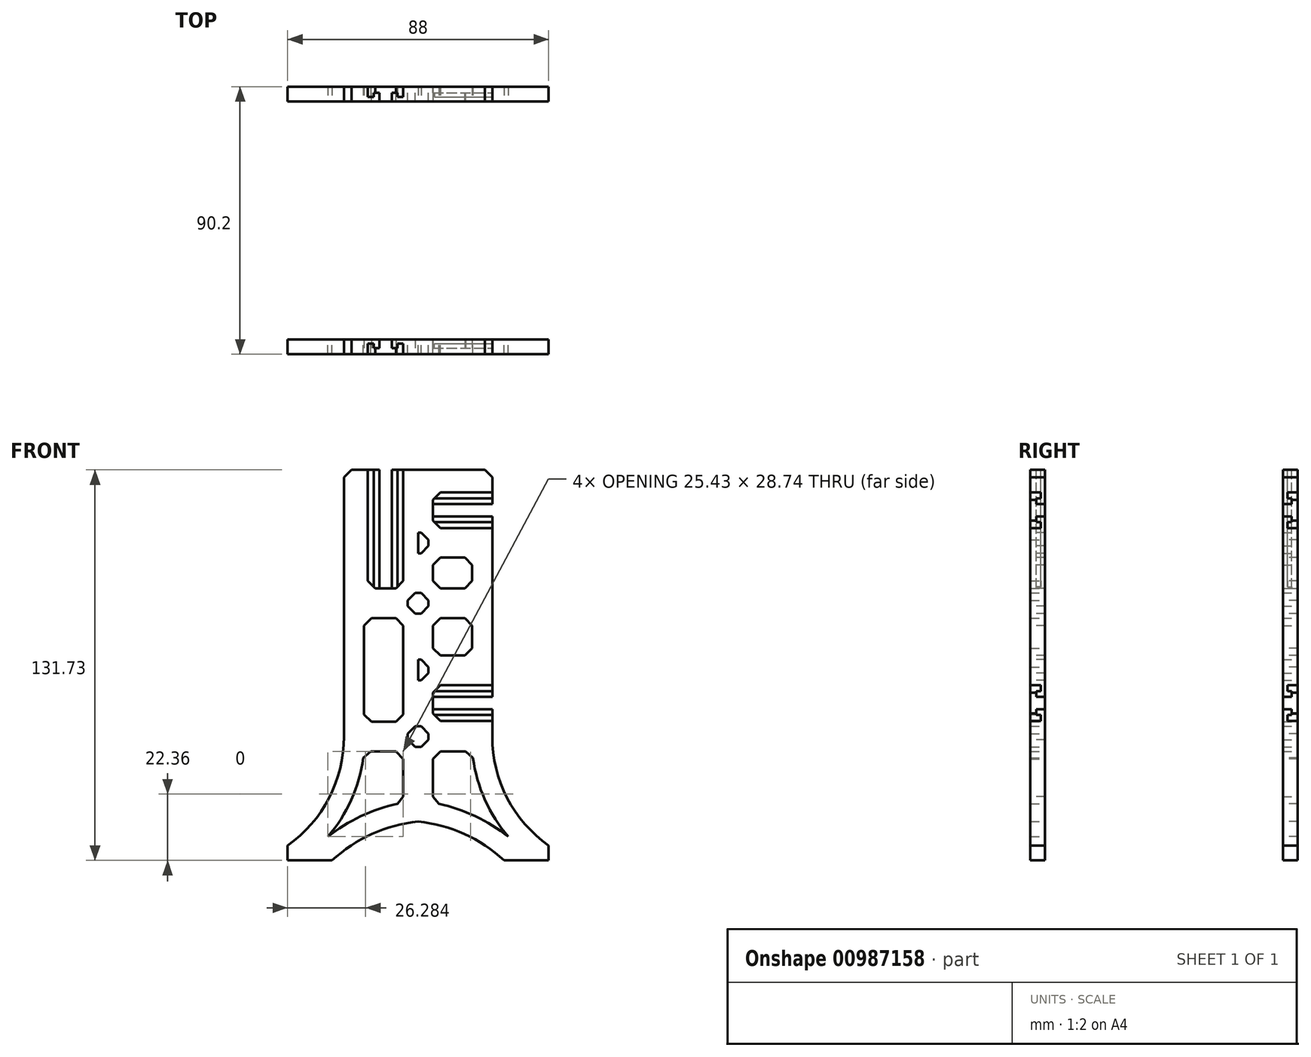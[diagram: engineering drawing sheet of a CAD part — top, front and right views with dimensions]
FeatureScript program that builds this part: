
annotation { "Feature Type Name" : "Feature", "Feature Type Description" : "" }
export const myFeature = defineFeature(function(context is Context, id is Id, definition is map)
    precondition{}
    {
        {
            var Q0;
            Q0=qCreatedBy(makeId("Front.planeOp"),FACE);
            var sketch = newSketch(context, id + "F0", { "sketchPlane" : qUnion([Q0])});
            skLineSegment(sketch, "E0", {"start": v(0, 90) * mm, "end": v(-25, 90) * mm});
            skLineSegment(sketch, "E1", {"start": v(-25, 90) * mm, "end": v(-25, 0) * mm});
            skLineSegment(sketch, "E2", {"start": v(-44, -41.73) * mm, "end": v(-29, -41.73) * mm});
            skLineSegment(sketch, "E3", {"start": v(-44, -41.73) * mm, "end": v(-44, -36.73) * mm});
            skArc(sketch, "E4", {"start": v(-25, 0) * mm, "mid": v(-30.03, -20.68) * mm, "end": v(-44, -36.73) * mm});
            skArc(sketch, "E5", {"start": v(0, -28.64) * mm, "mid": v(-15.57, -32.82) * mm, "end": v(-29, -41.73) * mm});
            skArc(sketch, "E6.0", {"start": v(-18.24, -5) * mm, "mid": v(-22.13, -20.3) * mm, "end": v(-30.43, -33.74) * mm});
            skArc(sketch, "E7.0", {"start": v(-5, -22.27) * mm, "mid": v(-18.43, -26.43) * mm, "end": v(-30.43, -33.74) * mm});
            skLineSegment(sketch, "E8", {"start": v(-18.24, -5) * mm, "end": v(-5, -5) * mm});
            skLineSegment(sketch, "E9", {"start": v(-5, -5) * mm, "end": v(-5, -22.27) * mm});
            skLineSegment(sketch, "E10", {"start": v(0, -28.64) * mm, "end": v(0, 90) * mm});
            skSolve(sketch);
        }
        {
            var Q0;
            Q0=makeQuery(id+"F0.imprint","IMPRINT",FACE,{"disambiguationData":[TD([[makeQuery(id+"F0.imprint","IMPRINT",EDGE,{"derivedFrom":sQuery(id+"F0.wireOp",EDGE,"E0")}),1.0]])]});
            extrude(context, id + "F1", {"entities" : qUnion([Q0]), "depth" : 5 * mm, "offsetDistance" : 25 * mm});
        }
        {
            var Q0;
            Q0=makeQuery(id+"F1.opExtrude","SWEPT_BODY",BODY,{"disambiguationData":[OSD([sQuery(id+"F0.wireOp",EDGE,"E0"),sQuery(id+"F0.wireOp",EDGE,"E1"),sQuery(id+"F0.wireOp",EDGE,"E2"),sQuery(id+"F0.wireOp",EDGE,"E3"),sQuery(id+"F0.wireOp",EDGE,"E4"),sQuery(id+"F0.wireOp",EDGE,"E5"),sQuery(id+"F0.wireOp",EDGE,"E6.0"),sQuery(id+"F0.wireOp",EDGE,"E7.0"),sQuery(id+"F0.wireOp",EDGE,"E8"),sQuery(id+"F0.wireOp",EDGE,"E9"),sQuery(id+"F0.wireOp",EDGE,"E10")])]});
            var Q1;
            Q1=qCreatedBy(makeId("Right.planeOp"),FACE);
            mirror(context, id + "F2", {"operationType" : NewBodyOperationType.ADD, "entities" : qUnion([Q0]), "mirrorPlane" : qUnion([Q1])});
        }
        {
            var Q0;
            Q0=makeQuery(id+"F2.opPattern","COPY",FACE,{"derivedFrom":makeQuery(id+"F1.opExtrude","SWEPT_FACE",FACE,{"disambiguationData":[OSD([sQuery(id+"F0.wireOp",EDGE,"E1")])]}),"instanceName":"1"});
            var sketch = newSketch(context, id + "F3", { "sketchPlane" : qUnion([Q0])});
            skLineSegment(sketch, "E11", {"start": v(0, 11.37) * mm, "end": v(-5, 11.37) * mm, "construction": true});
            skLineSegment(sketch, "E12", {"start": v(-5, 11.37) * mm, "end": v(-5, 17.37) * mm});
            skLineSegment(sketch, "E13", {"start": v(-5, 17.37) * mm, "end": v(-1.5, 17.37) * mm});
            skLineSegment(sketch, "E14", {"start": v(-1.5, 17.37) * mm, "end": v(-1.5, 15.37) * mm});
            skLineSegment(sketch, "E15", {"start": v(-1.5, 15.37) * mm, "end": v(-3, 15.37) * mm});
            skLineSegment(sketch, "E16", {"start": v(-3, 15.37) * mm, "end": v(-3, 13.47) * mm});
            skLineSegment(sketch, "E17", {"start": v(-3, 13.47) * mm, "end": v(0, 13.47) * mm});
            skLineSegment(sketch, "E18", {"start": v(0, 13.47) * mm, "end": v(0, 11.37) * mm});
            skLineSegment(sketch, "E19.MirrorCS", {"start": v(-3, 9.27) * mm, "end": v(0, 9.27) * mm});
            skLineSegment(sketch, "E20.MirrorCS", {"start": v(0, 9.27) * mm, "end": v(0, 11.37) * mm});
            skLineSegment(sketch, "E21.MirrorCS", {"start": v(-5, 5.37) * mm, "end": v(-1.5, 5.37) * mm});
            skLineSegment(sketch, "E22.MirrorCS", {"start": v(-5, 11.37) * mm, "end": v(-5, 5.37) * mm});
            skLineSegment(sketch, "E23.MirrorCS", {"start": v(-3, 7.37) * mm, "end": v(-3, 9.27) * mm});
            skLineSegment(sketch, "E24.MirrorCS", {"start": v(-1.5, 5.37) * mm, "end": v(-1.5, 7.37) * mm});
            skLineSegment(sketch, "E25.MirrorCS", {"start": v(-1.5, 7.37) * mm, "end": v(-3, 7.37) * mm});
            skLineSegment(sketch, "E26.0.1.0", {"start": v(-5, 76.37) * mm, "end": v(-5, 70.37) * mm});
            skLineSegment(sketch, "E26.0.1.1", {"start": v(-3, 74.27) * mm, "end": v(0, 74.27) * mm});
            skLineSegment(sketch, "E26.0.1.2", {"start": v(0, 76.37) * mm, "end": v(-5, 76.37) * mm, "construction": true});
            skLineSegment(sketch, "E26.0.1.3", {"start": v(-5, 82.37) * mm, "end": v(-1.5, 82.37) * mm});
            skLineSegment(sketch, "E26.0.1.4", {"start": v(-5, 76.37) * mm, "end": v(-5, 82.37) * mm});
            skLineSegment(sketch, "E26.0.1.5", {"start": v(-5, 70.37) * mm, "end": v(-1.5, 70.37) * mm});
            skLineSegment(sketch, "E26.0.1.6", {"start": v(-3, 78.47) * mm, "end": v(0, 78.47) * mm});
            skLineSegment(sketch, "E26.0.1.7", {"start": v(-1.5, 70.37) * mm, "end": v(-1.5, 72.37) * mm});
            skLineSegment(sketch, "E26.0.1.8", {"start": v(0, 74.27) * mm, "end": v(0, 76.37) * mm});
            skLineSegment(sketch, "E26.0.1.9", {"start": v(-3, 80.37) * mm, "end": v(-3, 78.47) * mm});
            skLineSegment(sketch, "E26.0.1.10", {"start": v(-3, 72.37) * mm, "end": v(-3, 74.27) * mm});
            skLineSegment(sketch, "E26.0.1.11", {"start": v(0, 78.47) * mm, "end": v(0, 76.37) * mm});
            skLineSegment(sketch, "E26.0.1.12", {"start": v(-1.5, 82.37) * mm, "end": v(-1.5, 80.37) * mm});
            skLineSegment(sketch, "E26.0.1.13", {"start": v(-1.5, 72.37) * mm, "end": v(-3, 72.37) * mm});
            skLineSegment(sketch, "E26.0.1.14", {"start": v(-1.5, 80.37) * mm, "end": v(-3, 80.37) * mm});
            skLineSegment(sketch, "E26.direction1", {"start": v(-5, 5.37) * mm, "end": v(20, 5.37) * mm, "construction": true});
            skLineSegment(sketch, "E26.direction2", {"start": v(-5, 5.37) * mm, "end": v(-5, 70.37) * mm, "construction": true});
            skSolve(sketch);
        }
        {
            var Q0;
            Q0=makeQuery(id+"F3.imprint","IMPRINT",FACE,{"disambiguationData":[TD([[makeQuery(id+"F3.imprint","IMPRINT",EDGE,{"derivedFrom":sQuery(id+"F3.wireOp",EDGE,"E26.0.1.0")}),1.0]])]});
            var Q1;
            Q1=makeQuery(id+"F3.imprint","IMPRINT",FACE,{"disambiguationData":[TD([[makeQuery(id+"F3.imprint","IMPRINT",EDGE,{"derivedFrom":sQuery(id+"F3.wireOp",EDGE,"E12")}),1.0]])]});
            extrude(context, id + "F4", {"entities" : qUnion([Q0, Q1]), "operationType" : NewBodyOperationType.REMOVE, "oppositeDirection" : true, "depth" : 20 * mm, "offsetDistance" : 25 * mm});
        }
        {
            var Q0;
            {var subQ0=makeQuery(id+"F1.opExtrude","SWEPT_FACE",FACE,{"disambiguationData":[OSD([sQuery(id+"F0.wireOp",EDGE,"E0")])]});Q0=makeQuery(id+"F2.boolean.opBoolean","MERGE",FACE,{"derivedFrom":[subQ0,makeQuery(id+"F2.opPattern","COPY",FACE,{"derivedFrom":subQ0,"instanceName":"1"})]});}
            var sketch = newSketch(context, id + "F5", { "sketchPlane" : qUnion([Q0])});
            skLineSegment(sketch, "E27", {"start": v(-17, -1.5) * mm, "end": v(-17, -5) * mm});
            skLineSegment(sketch, "E28", {"start": v(-17, -5) * mm, "end": v(-11, -5) * mm});
            skLineSegment(sketch, "E29", {"start": v(-11, -5) * mm, "end": v(-11, 0) * mm, "construction": true});
            skLineSegment(sketch, "E30", {"start": v(-11, 0) * mm, "end": v(-13.1, 0) * mm});
            skLineSegment(sketch, "E31", {"start": v(-13.1, 0) * mm, "end": v(-13.1, -3) * mm});
            skLineSegment(sketch, "E32", {"start": v(-13.1, -3) * mm, "end": v(-15, -3) * mm});
            skLineSegment(sketch, "E33", {"start": v(-15, -3) * mm, "end": v(-15, -1.5) * mm});
            skLineSegment(sketch, "E34", {"start": v(-15, -1.5) * mm, "end": v(-17, -1.5) * mm});
            skLineSegment(sketch, "E35.MirrorCS", {"start": v(-8.9, 0) * mm, "end": v(-8.9, -3) * mm});
            skLineSegment(sketch, "E36.MirrorCS", {"start": v(-7, -3) * mm, "end": v(-7, -1.5) * mm});
            skLineSegment(sketch, "E37.MirrorCS", {"start": v(-5, -5) * mm, "end": v(-11, -5) * mm});
            skLineSegment(sketch, "E38.MirrorCS", {"start": v(-11, 0) * mm, "end": v(-8.9, 0) * mm});
            skLineSegment(sketch, "E39.MirrorCS", {"start": v(-8.9, -3) * mm, "end": v(-7, -3) * mm});
            skLineSegment(sketch, "E40.MirrorCS", {"start": v(-7, -1.5) * mm, "end": v(-5, -1.5) * mm});
            skLineSegment(sketch, "E41.MirrorCS", {"start": v(-5, -1.5) * mm, "end": v(-5, -5) * mm});
            skSolve(sketch);
        }
        {
            var Q0;
            Q0=makeQuery(id+"F5.imprint","IMPRINT",FACE,{"disambiguationData":[TD([[makeQuery(id+"F5.imprint","IMPRINT",EDGE,{"derivedFrom":sQuery(id+"F5.wireOp",EDGE,"E27")}),1.0]])]});
            extrude(context, id + "F6", {"entities" : qUnion([Q0]), "operationType" : NewBodyOperationType.REMOVE, "oppositeDirection" : true, "depth" : 40 * mm, "offsetDistance" : 25 * mm});
        }
        {
            var Q0;
            {var subQ0=makeQuery(id+"F1.opExtrude","CAP_FACE",FACE,{"disambiguationData":[OSD([sQuery(id+"F0.wireOp",EDGE,"E0"),sQuery(id+"F0.wireOp",EDGE,"E1"),sQuery(id+"F0.wireOp",EDGE,"E2"),sQuery(id+"F0.wireOp",EDGE,"E3"),sQuery(id+"F0.wireOp",EDGE,"E4"),sQuery(id+"F0.wireOp",EDGE,"E5"),sQuery(id+"F0.wireOp",EDGE,"E6.0"),sQuery(id+"F0.wireOp",EDGE,"E7.0"),sQuery(id+"F0.wireOp",EDGE,"E8"),sQuery(id+"F0.wireOp",EDGE,"E9"),sQuery(id+"F0.wireOp",EDGE,"E10")])],"isStart":false});Q0=makeQuery(id+"F2.boolean.opBoolean","MERGE",FACE,{"derivedFrom":[subQ0,makeQuery(id+"F2.opPattern","COPY",FACE,{"derivedFrom":subQ0,"instanceName":"1"})]});}
            var sketch = newSketch(context, id + "F7", { "sketchPlane" : qUnion([Q0])});
            skLineSegment(sketch, "E42.bottom", {"start": v(-18.24, 5) * mm, "end": v(-5, 5) * mm});
            skLineSegment(sketch, "E42.top", {"start": v(-18.24, 40) * mm, "end": v(-5, 40) * mm});
            skLineSegment(sketch, "E42.left", {"start": v(-18.24, 5) * mm, "end": v(-18.24, 40) * mm});
            skLineSegment(sketch, "E42.right", {"start": v(-5, 5) * mm, "end": v(-5, 40) * mm});
            skLineSegment(sketch, "E43.bottom", {"start": v(5, 40) * mm, "end": v(18.24, 40) * mm});
            skLineSegment(sketch, "E43.top", {"start": v(5, 27.37) * mm, "end": v(18.24, 27.37) * mm});
            skLineSegment(sketch, "E43.left", {"start": v(5, 40) * mm, "end": v(5, 27.37) * mm});
            skLineSegment(sketch, "E43.right", {"start": v(18.24, 40) * mm, "end": v(18.24, 27.37) * mm});
            skLineSegment(sketch, "E44.bottom", {"start": v(5, 60.37) * mm, "end": v(18.24, 60.37) * mm});
            skLineSegment(sketch, "E44.top", {"start": v(5, 50) * mm, "end": v(18.24, 50) * mm});
            skLineSegment(sketch, "E44.left", {"start": v(5, 60.37) * mm, "end": v(5, 50) * mm});
            skLineSegment(sketch, "E44.right", {"start": v(18.24, 60.37) * mm, "end": v(18.24, 50) * mm});
            skLineSegment(sketch, "E45.bottom", {"start": v(3.5, 41.5) * mm, "end": v(-3.5, 41.5) * mm});
            skLineSegment(sketch, "E45.top", {"start": v(3.5, 48.5) * mm, "end": v(-3.5, 48.5) * mm});
            skLineSegment(sketch, "E45.left", {"start": v(3.5, 41.5) * mm, "end": v(3.5, 48.5) * mm});
            skLineSegment(sketch, "E45.right", {"start": v(-3.5, 41.5) * mm, "end": v(-3.5, 48.5) * mm});
            skPoint(sketch, "E45.middle", {"position": v(0, 45) * mm});
            skLineSegment(sketch, "E46", {"start": v(-5, 22.5) * mm, "end": v(-18.24, 22.5) * mm, "construction": true});
            skLineSegment(sketch, "E47.MirrorCS", {"start": v(3.5, 3.5) * mm, "end": v(3.5, -3.5) * mm});
            skPoint(sketch, "E48.MirrorP", {"position": v(0, 0) * mm});
            skLineSegment(sketch, "E49.MirrorCS", {"start": v(3.5, 3.5) * mm, "end": v(-3.5, 3.5) * mm});
            skLineSegment(sketch, "E50.MirrorCS", {"start": v(3.5, -3.5) * mm, "end": v(-3.5, -3.5) * mm});
            skLineSegment(sketch, "E51.MirrorCS", {"start": v(-3.5, 3.5) * mm, "end": v(-3.5, -3.5) * mm});
            skLineSegment(sketch, "E52.bottom", {"start": v(0, 26) * mm, "end": v(3.5, 26) * mm});
            skLineSegment(sketch, "E52.top", {"start": v(0, 19) * mm, "end": v(3.5, 19) * mm});
            skLineSegment(sketch, "E52.left", {"start": v(0, 26) * mm, "end": v(0, 19) * mm});
            skLineSegment(sketch, "E52.right", {"start": v(3.5, 26) * mm, "end": v(3.5, 19) * mm});
            skPoint(sketch, "E53", {"position": v(0, 22.5) * mm});
            skLineSegment(sketch, "E54.bottom", {"start": v(0, 68.87) * mm, "end": v(3.5, 68.87) * mm});
            skLineSegment(sketch, "E54.top", {"start": v(0, 61.87) * mm, "end": v(3.5, 61.87) * mm});
            skLineSegment(sketch, "E54.left", {"start": v(0, 68.87) * mm, "end": v(0, 61.87) * mm});
            skLineSegment(sketch, "E54.right", {"start": v(3.5, 68.87) * mm, "end": v(3.5, 61.87) * mm});
            skPoint(sketch, "E55", {"position": v(0, 65.37) * mm});
            skSolve(sketch);
        }
        {
            var Q0;
            Q0=makeQuery(id+"F7.imprint","IMPRINT",FACE,{"disambiguationData":[TD([[makeQuery(id+"F7.imprint","IMPRINT",EDGE,{"derivedFrom":sQuery(id+"F7.wireOp",EDGE,"E42.bottom")}),1.0]])]});
            var Q1;
            Q1=makeQuery(id+"F7.imprint","IMPRINT",FACE,{"disambiguationData":[TD([[makeQuery(id+"F7.imprint","IMPRINT",EDGE,{"derivedFrom":sQuery(id+"F7.wireOp",EDGE,"E43.bottom")}),-1.0]])]});
            var Q2;
            Q2=makeQuery(id+"F7.imprint","IMPRINT",FACE,{"disambiguationData":[TD([[makeQuery(id+"F7.imprint","IMPRINT",EDGE,{"derivedFrom":sQuery(id+"F7.wireOp",EDGE,"E44.bottom")}),-1.0]])]});
            var Q3;
            Q3=makeQuery(id+"F7.imprint","IMPRINT",FACE,{"disambiguationData":[TD([[makeQuery(id+"F7.imprint","IMPRINT",EDGE,{"derivedFrom":sQuery(id+"F7.wireOp",EDGE,"E45.bottom")}),-1.0]])]});
            var Q4;
            Q4=makeQuery(id+"F7.imprint","IMPRINT",FACE,{"disambiguationData":[TD([[makeQuery(id+"F7.imprint","IMPRINT",EDGE,{"derivedFrom":sQuery(id+"F7.wireOp",EDGE,"E47.MirrorCS")}),-1.0]])]});
            var Q5;
            Q5=makeQuery(id+"F7.imprint","IMPRINT",FACE,{"disambiguationData":[TD([[makeQuery(id+"F7.imprint","IMPRINT",EDGE,{"derivedFrom":sQuery(id+"F7.wireOp",EDGE,"E54.bottom")}),-1.0]])]});
            var Q6;
            Q6=makeQuery(id+"F7.imprint","IMPRINT",FACE,{"disambiguationData":[TD([[makeQuery(id+"F7.imprint","IMPRINT",EDGE,{"derivedFrom":sQuery(id+"F7.wireOp",EDGE,"E52.bottom")}),-1.0]])]});
            extrude(context, id + "F8", {"entities" : qUnion([Q0, Q1, Q2, Q3, Q4, Q5, Q6]), "operationType" : NewBodyOperationType.REMOVE, "endBound" : BoundingType.THROUGH_ALL, "oppositeDirection" : true, "depth" : 25 * mm, "offsetDistance" : 25 * mm});
        }
        {
            var Q0;
            Q0=makeQuery(id+"F1.opExtrude","SWEPT_EDGE",EDGE,{"disambiguationData":[OSD([sQuery(id+"F0.wireOp",EDGE,"E8"),sQuery(id+"F0.wireOp",EDGE,"E9")])]});
            var Q1;
            Q1=makeQuery(id+"F1.opExtrude","SWEPT_EDGE",EDGE,{"disambiguationData":[OSD([sQuery(id+"F0.wireOp",EDGE,"E6.0"),sQuery(id+"F0.wireOp",EDGE,"E8")])]});
            var Q2;
            Q2=makeQuery(id+"F1.opExtrude","SWEPT_EDGE",EDGE,{"disambiguationData":[OSD([sQuery(id+"F0.wireOp",EDGE,"E7.0"),sQuery(id+"F0.wireOp",EDGE,"E9")])]});
            var Q3;
            Q3=makeQuery(id+"F2.opPattern","COPY",EDGE,{"derivedFrom":makeQuery(id+"F1.opExtrude","SWEPT_EDGE",EDGE,{"disambiguationData":[OSD([sQuery(id+"F0.wireOp",EDGE,"E7.0"),sQuery(id+"F0.wireOp",EDGE,"E9")])]}),"instanceName":"1"});
            var Q4;
            Q4=makeQuery(id+"F2.opPattern","COPY",EDGE,{"derivedFrom":makeQuery(id+"F1.opExtrude","SWEPT_EDGE",EDGE,{"disambiguationData":[OSD([sQuery(id+"F0.wireOp",EDGE,"E8"),sQuery(id+"F0.wireOp",EDGE,"E9")])]}),"instanceName":"1"});
            var Q5;
            Q5=makeQuery(id+"F2.opPattern","COPY",EDGE,{"derivedFrom":makeQuery(id+"F1.opExtrude","SWEPT_EDGE",EDGE,{"disambiguationData":[OSD([sQuery(id+"F0.wireOp",EDGE,"E6.0"),sQuery(id+"F0.wireOp",EDGE,"E8")])]}),"instanceName":"1"});
            var Q6;
            Q6=makeQuery(id+"F8.boolean.opBoolean","COPY",EDGE,{"derivedFrom":makeQuery(id+"F8.opExtrude","SWEPT_EDGE",EDGE,{"disambiguationData":[OSD([sQuery(id+"F7.wireOp",EDGE,"E42.bottom"),sQuery(id+"F7.wireOp",EDGE,"E42.right")])]})});
            var Q7;
            Q7=makeQuery(id+"F8.boolean.opBoolean","COPY",EDGE,{"derivedFrom":makeQuery(id+"F8.opExtrude","SWEPT_EDGE",EDGE,{"disambiguationData":[OSD([sQuery(id+"F7.wireOp",EDGE,"E42.bottom"),sQuery(id+"F7.wireOp",EDGE,"E42.left")])]})});
            var Q8;
            Q8=makeQuery(id+"F8.boolean.opBoolean","COPY",EDGE,{"derivedFrom":makeQuery(id+"F8.opExtrude","SWEPT_EDGE",EDGE,{"disambiguationData":[OSD([sQuery(id+"F7.wireOp",EDGE,"E42.top"),sQuery(id+"F7.wireOp",EDGE,"E42.left")])]})});
            var Q9;
            Q9=makeQuery(id+"F8.boolean.opBoolean","COPY",EDGE,{"derivedFrom":makeQuery(id+"F8.opExtrude","SWEPT_EDGE",EDGE,{"disambiguationData":[OSD([sQuery(id+"F7.wireOp",EDGE,"E42.top"),sQuery(id+"F7.wireOp",EDGE,"E42.right")])]})});
            var Q10;
            Q10=makeQuery(id+"F8.boolean.opBoolean","COPY",EDGE,{"derivedFrom":makeQuery(id+"F8.opExtrude","SWEPT_EDGE",EDGE,{"disambiguationData":[OSD([sQuery(id+"F7.wireOp",EDGE,"E43.bottom"),sQuery(id+"F7.wireOp",EDGE,"E43.left")])]})});
            var Q11;
            Q11=makeQuery(id+"F8.boolean.opBoolean","COPY",EDGE,{"derivedFrom":makeQuery(id+"F8.opExtrude","SWEPT_EDGE",EDGE,{"disambiguationData":[OSD([sQuery(id+"F7.wireOp",EDGE,"E44.top"),sQuery(id+"F7.wireOp",EDGE,"E44.left")])]})});
            var Q12;
            Q12=makeQuery(id+"F8.boolean.opBoolean","COPY",EDGE,{"derivedFrom":makeQuery(id+"F8.opExtrude","SWEPT_EDGE",EDGE,{"disambiguationData":[OSD([sQuery(id+"F7.wireOp",EDGE,"E44.bottom"),sQuery(id+"F7.wireOp",EDGE,"E44.left")])]})});
            var Q13;
            Q13=makeQuery(id+"F8.boolean.opBoolean","COPY",EDGE,{"derivedFrom":makeQuery(id+"F8.opExtrude","SWEPT_EDGE",EDGE,{"disambiguationData":[OSD([sQuery(id+"F7.wireOp",EDGE,"E44.bottom"),sQuery(id+"F7.wireOp",EDGE,"E44.right")])]})});
            var Q14;
            Q14=makeQuery(id+"F8.boolean.opBoolean","COPY",EDGE,{"derivedFrom":makeQuery(id+"F8.opExtrude","SWEPT_EDGE",EDGE,{"disambiguationData":[OSD([sQuery(id+"F7.wireOp",EDGE,"E44.top"),sQuery(id+"F7.wireOp",EDGE,"E44.right")])]})});
            var Q15;
            Q15=makeQuery(id+"F8.boolean.opBoolean","COPY",EDGE,{"derivedFrom":makeQuery(id+"F8.opExtrude","SWEPT_EDGE",EDGE,{"disambiguationData":[OSD([sQuery(id+"F7.wireOp",EDGE,"E43.bottom"),sQuery(id+"F7.wireOp",EDGE,"E43.right")])]})});
            var Q16;
            Q16=makeQuery(id+"F8.boolean.opBoolean","COPY",EDGE,{"derivedFrom":makeQuery(id+"F8.opExtrude","SWEPT_EDGE",EDGE,{"disambiguationData":[OSD([sQuery(id+"F7.wireOp",EDGE,"E43.top"),sQuery(id+"F7.wireOp",EDGE,"E43.right")])]})});
            var Q17;
            Q17=makeQuery(id+"F8.boolean.opBoolean","COPY",EDGE,{"derivedFrom":makeQuery(id+"F8.opExtrude","SWEPT_EDGE",EDGE,{"disambiguationData":[OSD([sQuery(id+"F7.wireOp",EDGE,"E43.top"),sQuery(id+"F7.wireOp",EDGE,"E43.left")])]})});
            var Q18;
            Q18=makeQuery(id+"F8.boolean.opBoolean","COPY",EDGE,{"derivedFrom":makeQuery(id+"F8.opExtrude","SWEPT_EDGE",EDGE,{"disambiguationData":[OSD([sQuery(id+"F7.wireOp",EDGE,"E45.bottom"),sQuery(id+"F7.wireOp",EDGE,"E45.right")])]})});
            var Q19;
            Q19=makeQuery(id+"F8.boolean.opBoolean","COPY",EDGE,{"derivedFrom":makeQuery(id+"F8.opExtrude","SWEPT_EDGE",EDGE,{"disambiguationData":[OSD([sQuery(id+"F7.wireOp",EDGE,"E45.top"),sQuery(id+"F7.wireOp",EDGE,"E45.right")])]})});
            var Q20;
            Q20=makeQuery(id+"F8.boolean.opBoolean","COPY",EDGE,{"derivedFrom":makeQuery(id+"F8.opExtrude","SWEPT_EDGE",EDGE,{"disambiguationData":[OSD([sQuery(id+"F7.wireOp",EDGE,"E45.top"),sQuery(id+"F7.wireOp",EDGE,"E45.left")])]})});
            var Q21;
            Q21=makeQuery(id+"F8.boolean.opBoolean","COPY",EDGE,{"derivedFrom":makeQuery(id+"F8.opExtrude","SWEPT_EDGE",EDGE,{"disambiguationData":[OSD([sQuery(id+"F7.wireOp",EDGE,"E45.bottom"),sQuery(id+"F7.wireOp",EDGE,"E45.left")])]})});
            var Q22;
            Q22=makeQuery(id+"F8.boolean.opBoolean","COPY",EDGE,{"derivedFrom":makeQuery(id+"F8.opExtrude","SWEPT_EDGE",EDGE,{"disambiguationData":[OSD([sQuery(id+"F7.wireOp",EDGE,"E49.MirrorCS"),sQuery(id+"F7.wireOp",EDGE,"E51.MirrorCS")])]})});
            var Q23;
            Q23=makeQuery(id+"F8.boolean.opBoolean","COPY",EDGE,{"derivedFrom":makeQuery(id+"F8.opExtrude","SWEPT_EDGE",EDGE,{"disambiguationData":[OSD([sQuery(id+"F7.wireOp",EDGE,"E47.MirrorCS"),sQuery(id+"F7.wireOp",EDGE,"E49.MirrorCS")])]})});
            var Q24;
            Q24=makeQuery(id+"F8.boolean.opBoolean","COPY",EDGE,{"derivedFrom":makeQuery(id+"F8.opExtrude","SWEPT_EDGE",EDGE,{"disambiguationData":[OSD([sQuery(id+"F7.wireOp",EDGE,"E47.MirrorCS"),sQuery(id+"F7.wireOp",EDGE,"E50.MirrorCS")])]})});
            var Q25;
            Q25=makeQuery(id+"F8.boolean.opBoolean","COPY",EDGE,{"derivedFrom":makeQuery(id+"F8.opExtrude","SWEPT_EDGE",EDGE,{"disambiguationData":[OSD([sQuery(id+"F7.wireOp",EDGE,"E50.MirrorCS"),sQuery(id+"F7.wireOp",EDGE,"E51.MirrorCS")])]})});
            var Q26;
            Q26=makeQuery(id+"F6.boolean.opBoolean","COPY",EDGE,{"derivedFrom":makeQuery(id+"F6.opExtrude","CAP_EDGE",EDGE,{"disambiguationData":[OSD([sQuery(id+"F5.wireOp",EDGE,"E27")])],"isStart":false})});
            var Q27;
            Q27=makeQuery(id+"F6.boolean.opBoolean","COPY",EDGE,{"derivedFrom":makeQuery(id+"F6.opExtrude","CAP_EDGE",EDGE,{"disambiguationData":[OSD([sQuery(id+"F5.wireOp",EDGE,"E41.MirrorCS")])],"isStart":false})});
            var Q28;
            Q28=makeQuery(id+"F4.boolean.opBoolean","COPY",EDGE,{"derivedFrom":makeQuery(id+"F4.opExtrude","CAP_EDGE",EDGE,{"disambiguationData":[OSD([sQuery(id+"F3.wireOp",EDGE,"E26.0.1.5")])],"isStart":false})});
            var Q29;
            Q29=makeQuery(id+"F4.boolean.opBoolean","COPY",EDGE,{"derivedFrom":makeQuery(id+"F4.opExtrude","CAP_EDGE",EDGE,{"disambiguationData":[OSD([sQuery(id+"F3.wireOp",EDGE,"E26.0.1.3")])],"isStart":false})});
            var Q30;
            Q30=makeQuery(id+"F4.boolean.opBoolean","COPY",EDGE,{"derivedFrom":makeQuery(id+"F4.opExtrude","CAP_EDGE",EDGE,{"disambiguationData":[OSD([sQuery(id+"F3.wireOp",EDGE,"E13")])],"isStart":false})});
            var Q31;
            Q31=makeQuery(id+"F4.boolean.opBoolean","COPY",EDGE,{"derivedFrom":makeQuery(id+"F4.opExtrude","CAP_EDGE",EDGE,{"disambiguationData":[OSD([sQuery(id+"F3.wireOp",EDGE,"E21.MirrorCS")])],"isStart":false})});
            var Q32;
            Q32=makeQuery(id+"F1.opExtrude","SWEPT_EDGE",EDGE,{"disambiguationData":[OSD([sQuery(id+"F0.wireOp",EDGE,"E0"),sQuery(id+"F0.wireOp",EDGE,"E1")])]});
            var Q33;
            Q33=makeQuery(id+"F2.opPattern","COPY",EDGE,{"derivedFrom":makeQuery(id+"F1.opExtrude","SWEPT_EDGE",EDGE,{"disambiguationData":[OSD([sQuery(id+"F0.wireOp",EDGE,"E0"),sQuery(id+"F0.wireOp",EDGE,"E1")])]}),"instanceName":"1"});
            var Q34;
            Q34=makeQuery(id+"F8.boolean.opBoolean","COPY",EDGE,{"derivedFrom":makeQuery(id+"F8.opExtrude","SWEPT_EDGE",EDGE,{"disambiguationData":[OSD([sQuery(id+"F7.wireOp",EDGE,"E52.bottom"),sQuery(id+"F7.wireOp",EDGE,"E52.right")])]})});
            var Q35;
            Q35=makeQuery(id+"F8.boolean.opBoolean","COPY",EDGE,{"derivedFrom":makeQuery(id+"F8.opExtrude","SWEPT_EDGE",EDGE,{"disambiguationData":[OSD([sQuery(id+"F7.wireOp",EDGE,"E52.top"),sQuery(id+"F7.wireOp",EDGE,"E52.right")])]})});
            var Q36;
            Q36=makeQuery(id+"F8.boolean.opBoolean","COPY",EDGE,{"derivedFrom":makeQuery(id+"F8.opExtrude","SWEPT_EDGE",EDGE,{"disambiguationData":[OSD([sQuery(id+"F7.wireOp",EDGE,"E54.bottom"),sQuery(id+"F7.wireOp",EDGE,"E54.right")])]})});
            var Q37;
            Q37=makeQuery(id+"F8.boolean.opBoolean","COPY",EDGE,{"derivedFrom":makeQuery(id+"F8.opExtrude","SWEPT_EDGE",EDGE,{"disambiguationData":[OSD([sQuery(id+"F7.wireOp",EDGE,"E54.top"),sQuery(id+"F7.wireOp",EDGE,"E54.right")])]})});
            chamfer(context, id + "F9", {"entities" : qUnion([Q0, Q1, Q2, Q3, Q4, Q5, Q6, Q7, Q8, Q9, Q10, Q11, Q12, Q13, Q14, Q15, Q16, Q17, Q18, Q19, Q20, Q21, Q22, Q23, Q24, Q25, Q26, Q27, Q28, Q29, Q30, Q31, Q32, Q33, Q34, Q35, Q36, Q37]), "width" : 2.5 * mm, "tangentPropagation" : true});
        }
        {
            var Q0;
            Q0=qCreatedBy(makeId("Front.planeOp"),FACE);
            cPlane(context, id + "F10", {"entities" : qUnion([Q0]), "cplaneType" : CPlaneType.OFFSET, "offset" : 40.1 * mm, "oppositeDirection" : true, "width" : 150 * mm, "height" : 150 * mm});
        }
        {
            var Q0;
            Q0=makeQuery(id+"F1.opExtrude","SWEPT_BODY",BODY,{"disambiguationData":[OSD([sQuery(id+"F0.wireOp",EDGE,"E0"),sQuery(id+"F0.wireOp",EDGE,"E1"),sQuery(id+"F0.wireOp",EDGE,"E2"),sQuery(id+"F0.wireOp",EDGE,"E3"),sQuery(id+"F0.wireOp",EDGE,"E4"),sQuery(id+"F0.wireOp",EDGE,"E5"),sQuery(id+"F0.wireOp",EDGE,"E6.0"),sQuery(id+"F0.wireOp",EDGE,"E7.0"),sQuery(id+"F0.wireOp",EDGE,"E8"),sQuery(id+"F0.wireOp",EDGE,"E9"),sQuery(id+"F0.wireOp",EDGE,"E10")])]});
            var Q1;
            Q1=qCreatedBy(id+"F10.planeOp",FACE);
            mirror(context, id + "F11", {"entities" : qUnion([Q0]), "mirrorPlane" : qUnion([Q1])});
        }
    });
